# Revit family: Reece_Bath_Decina_Isle MK2_Freestanding Spa Bath_1790 mm
name_source: partatom
category: Plumbing Fixtures
revit_build: Autodesk Revit 2018 (Build: 20190510_1515(x64)
units: mm (PartAtom-declared; Revit-internal decimal feet)

## family parameters
Cut with Voids When Loaded = Yes
Host = Face
Part Type = Normal
Room Calculation Point = Yes
Round Connector Dimension = Use Diameter
Shared = Yes

## types (1)
- 190 L_Acrylic_White
    Default Elevation = 0 mm  [stored 0 ft]
    Description = Decina Isle MK2 1790mm Freestanding 10 Jet Spa Bath
    Disclaimer = THIS FILE IS THE PROPERTY OF THE REECE GROUP. IT MAY NOT BE REPRODUCED, REVERSE-ENGINEERED OR MODIFIED. ANY REPUBLICATION, TRANSMISSION OR DISTRIBUTION FOR THE PURPOSE OF COMMERCIALLY EXPLOITING THE FILES IS PROHIBITED.
    Keynote = Product #9506049, Reece_Bath_Decina_Isle MK2_Freestanding Spa Bath_1790 mm - 190 L_Acrylic_White
    Manufacturer = Decina
    Model = Isle MK2
    Reece_Bath_Outlet = 40 mm  [stored 0.131234 ft]
    Reece_Detail_Additional = 10 Jet Spa
    Reece_Detail_Disclaimer = THIS FILE IS THE PROPERTY OF THE REECE GROUP. IT MAY NOT BE REPRODUCED, REVERSE-ENGINEERED OR MODIFIED. ANY REPUBLICATION, TRANSMISSION OR DISTRIBUTION FOR THE PURPOSE OF COMMERCIALLY EXPLOITING THE FILES IS PROHIBITED.
    Reece_Detail_Installation = Freestanding Spa Bath
    Reece_Material_Main = Reece_Acrylic_White
    Reece_Material_Secondary = Reece_Brass_Chrome
    Reece_Overall_Capacity = 190 L
    Reece_Overall_Height = 595 mm  [stored 1.9521 ft]
    Reece_Overall_Length = 1790 mm  [stored 5.8727 ft]
    Reece_Overall_Width = 900 mm  [stored 2.95276 ft]
    Reece_Product_Brand = Decina
    Reece_Product_Description = Decina Isle MK2 1790mm Freestanding 10 Jet Spa Bath
    Reece_Product_Mount = Floor Mounted
    Reece_Product_Number = 9506049
    Reece_Product_Sub Brand = Isle MK2
    Reece_Product_Type = Bath
    Reece_Product_Web Page = https://www.reece.com.au
    Type Comments = Bath
    URL = https://www.reece.com.au

note: [stored X ft] marks values corroborated as IEEE doubles in the binary element streams (Revit-internal decimal feet)

## geometry (parser evidence)
native form markers: Sweep x4
no freeform markers — native parametric forms only
